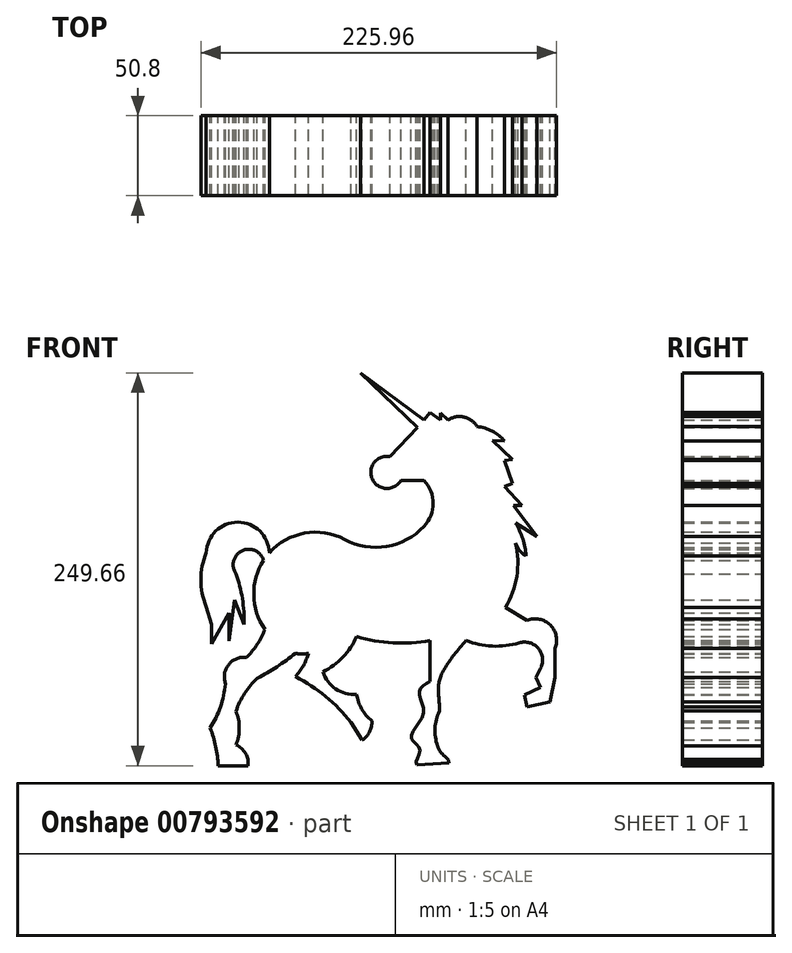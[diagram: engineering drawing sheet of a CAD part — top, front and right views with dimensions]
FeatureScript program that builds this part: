
annotation { "Feature Type Name" : "Feature", "Feature Type Description" : "" }
export const myFeature = defineFeature(function(context is Context, id is Id, definition is map)
    precondition{}
    {
        {
            var Q0;
            Q0=qCreatedBy(makeId("Front.planeOp"),FACE);
            var sketch = newSketch(context, id + "F0", { "sketchPlane" : qUnion([Q0])});
            skLineSegment(sketch, "E0", {"start": v(117.02, 256.9) * mm, "end": v(157.35, 226.79) * mm});
            skLineSegment(sketch, "E1", {"start": v(117.02, 256.9) * mm, "end": v(153.27, 222.2) * mm});
            skLineSegment(sketch, "E2", {"start": v(153.27, 222.2) * mm, "end": v(135.55, 203.69) * mm});
            skArc(sketch, "E3", {"start": v(135.55, 203.69) * mm, "mid": v(124.47, 189.38) * mm, "end": v(142.55, 188.5) * mm});
            skLineSegment(sketch, "E4", {"start": v(142.55, 188.5) * mm, "end": v(157.35, 188.5) * mm});
            skArc(sketch, "E5", {"start": v(157.35, 159.4) * mm, "mid": v(163.1, 173.94) * mm, "end": v(157.35, 188.5) * mm});
            skArc(sketch, "E6", {"start": v(106.85, 151.02) * mm, "mid": v(59.08, 142.48) * mm, "end": v(56.24, 94.04) * mm});
            skArc(sketch, "E7", {"start": v(106.85, 151.02) * mm, "mid": v(133.52, 146.63) * mm, "end": v(157.35, 159.4) * mm});
            skArc(sketch, "E8", {"start": v(208.92, 107.83) * mm, "mid": v(216.22, 127.6) * mm, "end": v(215.55, 148.67) * mm});
            skArc(sketch, "E9", {"start": v(183.9, 86.9) * mm, "mid": v(200.68, 83.25) * mm, "end": v(217.72, 85.39) * mm});
            skArc(sketch, "E10", {"start": v(231.43, 69.23) * mm, "mid": v(229.88, 81.8) * mm, "end": v(217.72, 85.39) * mm});
            skArc(sketch, "E11", {"start": v(240.57, 81.8) * mm, "mid": v(237.5, 96.6) * mm, "end": v(222.7, 99.66) * mm});
            skLineSegment(sketch, "E12", {"start": v(240.57, 81.8) * mm, "end": v(240.57, 63.41) * mm});
            skLineSegment(sketch, "E13", {"start": v(208.92, 107.83) * mm, "end": v(222.7, 99.66) * mm});
            skLineSegment(sketch, "E14", {"start": v(231.43, 69.23) * mm, "end": v(228.56, 63.41) * mm});
            skLineSegment(sketch, "E15", {"start": v(228.56, 63.41) * mm, "end": v(231.43, 57) * mm});
            skLineSegment(sketch, "E16", {"start": v(231.43, 57) * mm, "end": v(221.07, 52.36) * mm});
            skLineSegment(sketch, "E17", {"start": v(221.07, 52.36) * mm, "end": v(222.7, 44.75) * mm});
            skLineSegment(sketch, "E18", {"start": v(222.7, 44.75) * mm, "end": v(237.34, 47.87) * mm});
            skLineSegment(sketch, "E19", {"start": v(237.34, 47.87) * mm, "end": v(240.57, 63.41) * mm});
            skArc(sketch, "E20", {"start": v(59.08, 142.48) * mm, "mid": v(39.04, 161.99) * mm, "end": v(19, 142.48) * mm});
            skPoint(sketch, "E20.endSnap0", {"position": v(59.08, 142.48) * mm});
            skArc(sketch, "E21", {"start": v(55.46, 137.72) * mm, "mid": v(41.7, 143.82) * mm, "end": v(37.88, 129.27) * mm});
            skArc(sketch, "E22", {"start": v(19, 142.48) * mm, "mid": v(15.58, 125.41) * mm, "end": v(19, 108.34) * mm});
            skArc(sketch, "E23", {"start": v(44.52, 76.17) * mm, "mid": v(33.18, 71.46) * mm, "end": v(31.25, 59.33) * mm});
            skArc(sketch, "E24", {"start": v(114.47, 89.45) * mm, "mid": v(137.67, 85.34) * mm, "end": v(161.2, 86.84) * mm});
            skArc(sketch, "E25", {"start": v(93.02, 66.98) * mm, "mid": v(105.8, 76.26) * mm, "end": v(114.47, 89.45) * mm});
            skArc(sketch, "E26", {"start": v(93.02, 66.98) * mm, "mid": v(101.25, 56.1) * mm, "end": v(114.47, 52.69) * mm});
            skArc(sketch, "E27", {"start": v(114.47, 52.69) * mm, "mid": v(117.73, 43.35) * mm, "end": v(124.17, 35.84) * mm});
            skArc(sketch, "E28", {"start": v(118.04, 23.59) * mm, "mid": v(122.8, 28.87) * mm, "end": v(124.17, 35.84) * mm});
            skArc(sketch, "E29", {"start": v(167.05, 61.35) * mm, "mid": v(177.73, 72.64) * mm, "end": v(183.9, 86.9) * mm});
            skArc(sketch, "E30", {"start": v(167.05, 41.98) * mm, "mid": v(169.24, 51.67) * mm, "end": v(167.05, 61.35) * mm});
            skArc(sketch, "E31", {"start": v(167.05, 41.98) * mm, "mid": v(164.24, 29.59) * mm, "end": v(167.05, 17.2) * mm});
            skArc(sketch, "E32", {"start": v(173.17, 9.02) * mm, "mid": v(171.2, 13.93) * mm, "end": v(167.05, 17.2) * mm});
            skLineSegment(sketch, "E33", {"start": v(152.75, 7.8) * mm, "end": v(173.17, 9.02) * mm});
            skLineSegment(sketch, "E34", {"start": v(161.2, 86.84) * mm, "end": v(161.2, 60.95) * mm});
            skFitSpline(sketch, "E35", {"points": [v(161.2, 60.95) * mm, v(154.29, 54.22) * mm, v(156.84, 40.44) * mm, v(149.18, 25.12) * mm, v(154.8, 17.46) * mm, v(152.75, 7.8) * mm, v(173.17, 9.02) * mm, v(167.05, 17.2) * mm, v(167.05, 41.98) * mm, v(167.05, 61.35) * mm, v(183.9, 86.9) * mm], "startDerivative": vector(-126.82, -72.82) * mm, "endDerivative": vector(160.9, 190.3) * mm});
            skArc(sketch, "E36", {"start": v(44.52, 76.17) * mm, "mid": v(51.4, 84.44) * mm, "end": v(56.24, 94.04) * mm});
            skArc(sketch, "E37", {"start": v(21.55, 31.25) * mm, "mid": v(28.01, 44.73) * mm, "end": v(31.25, 59.33) * mm});
            skArc(sketch, "E38", {"start": v(26.65, 7.25) * mm, "mid": v(25.03, 19.45) * mm, "end": v(21.55, 31.25) * mm});
            skLineSegment(sketch, "E39", {"start": v(26.65, 7.25) * mm, "end": v(45.54, 7.25) * mm});
            skArc(sketch, "E40", {"start": v(51.4, 62.9) * mm, "mid": v(63.94, 70.18) * mm, "end": v(75.66, 78.73) * mm});
            skPoint(sketch, "E40.startSnap0", {"position": v(51.4, 84.44) * mm});
            skArc(sketch, "E41", {"start": v(75.66, 78.73) * mm, "mid": v(79.75, 78.22) * mm, "end": v(83.83, 78.73) * mm});
            skArc(sketch, "E42", {"start": v(75.66, 63.92) * mm, "mid": v(80.62, 70.84) * mm, "end": v(83.83, 78.73) * mm});
            skArc(sketch, "E43", {"start": v(110.9, 34.82) * mm, "mid": v(94.88, 51.31) * mm, "end": v(75.66, 63.92) * mm});
            skLineSegment(sketch, "E44", {"start": v(110.9, 34.82) * mm, "end": v(118.04, 23.59) * mm});
            skArc(sketch, "E45", {"start": v(51.4, 62.9) * mm, "mid": v(43.37, 53.26) * mm, "end": v(37.88, 41.97) * mm});
            skArc(sketch, "E46", {"start": v(37.88, 20.52) * mm, "mid": v(39.97, 31.25) * mm, "end": v(37.88, 41.97) * mm});
            skArc(sketch, "E47", {"start": v(45.54, 7.25) * mm, "mid": v(43.99, 15.2) * mm, "end": v(37.88, 20.52) * mm});
            skArc(sketch, "E48", {"start": v(215.55, 148.67) * mm, "mid": v(218.09, 143.95) * mm, "end": v(222.2, 140.5) * mm});
            skArc(sketch, "E49", {"start": v(222.2, 140.5) * mm, "mid": v(220.05, 151.34) * mm, "end": v(215.55, 161.44) * mm});
            skLineSegment(sketch, "E50", {"start": v(157.35, 226.79) * mm, "end": v(161.08, 231.77) * mm});
            skLineSegment(sketch, "E51", {"start": v(161.08, 231.77) * mm, "end": v(167.75, 226.79) * mm});
            skLineSegment(sketch, "E52", {"start": v(167.75, 226.79) * mm, "end": v(167.75, 231.38) * mm});
            skLineSegment(sketch, "E53", {"start": v(167.75, 231.38) * mm, "end": v(172.55, 226.79) * mm});
            skArc(sketch, "E54", {"start": v(191.05, 222.7) * mm, "mid": v(182.7, 228.81) * mm, "end": v(172.55, 226.79) * mm});
            skArc(sketch, "E55", {"start": v(208.4, 213.51) * mm, "mid": v(200.64, 219.82) * mm, "end": v(191.05, 222.7) * mm});
            skLineSegment(sketch, "E56", {"start": v(200.64, 214.02) * mm, "end": v(208.4, 213.51) * mm});
            skPoint(sketch, "E56.startSnap0", {"position": v(200.64, 219.82) * mm});
            skLineSegment(sketch, "E57", {"start": v(200.64, 214.02) * mm, "end": v(213.51, 201.77) * mm});
            skLineSegment(sketch, "E58", {"start": v(213.51, 201.77) * mm, "end": v(208.4, 201.31) * mm});
            skLineSegment(sketch, "E59", {"start": v(208.4, 201.31) * mm, "end": v(213.51, 186.45) * mm});
            skLineSegment(sketch, "E60", {"start": v(213.51, 186.45) * mm, "end": v(208.4, 184.7) * mm});
            skLineSegment(sketch, "E61", {"start": v(208.4, 184.7) * mm, "end": v(219.64, 172.67) * mm});
            skLineSegment(sketch, "E62", {"start": v(219.64, 172.67) * mm, "end": v(214.02, 172.67) * mm});
            skPoint(sketch, "E62.endSnap0", {"position": v(214.02, 178.68) * mm});
            skLineSegment(sketch, "E63", {"start": v(214.02, 172.67) * mm, "end": v(229.08, 152.88) * mm});
            skLineSegment(sketch, "E64", {"start": v(229.08, 152.88) * mm, "end": v(215.55, 161.44) * mm});
            skArc(sketch, "E65", {"start": v(43.12, 97.11) * mm, "mid": v(41.95, 113.43) * mm, "end": v(37.88, 129.27) * mm});
            skLineSegment(sketch, "E66", {"start": v(43.12, 97.11) * mm, "end": v(36.91, 112.47) * mm});
            skLineSegment(sketch, "E67", {"start": v(36.91, 112.47) * mm, "end": v(33.45, 86.7) * mm});
            skLineSegment(sketch, "E68", {"start": v(33.45, 86.7) * mm, "end": v(33.45, 104.26) * mm});
            skLineSegment(sketch, "E69", {"start": v(33.45, 104.26) * mm, "end": v(22.3, 84.75) * mm});
            skLineSegment(sketch, "E70", {"start": v(22.3, 84.75) * mm, "end": v(22.3, 97.11) * mm});
            skLineSegment(sketch, "E71", {"start": v(22.3, 97.11) * mm, "end": v(19, 108.34) * mm});
            skSolve(sketch);
        }
        {
            var Q0;
            Q0=makeQuery(id+"F0.imprint","IMPRINT",FACE,{"disambiguationData":[TD([[makeQuery(id+"F0.imprint","IMPRINT",EDGE,{"derivedFrom":sQuery(id+"F0.wireOp",EDGE,"E0")}),-1.0]])]});
            var Q1;
            {var subQ0=sQuery(id+"F0.wireOp",EDGE,"E20");Q1=makeQuery(id+"F0.imprint","IMPRINT",FACE,{"disambiguationData":[TD([[makeQuery(id+"F0.imprint","IMPRINT",EDGE,{"derivedFrom":subQ0}),1.0]])]});}
            extrude(context, id + "F1", {"entities" : qUnion([Q0, Q1]), "depth" : 50.8 * mm, "offsetDistance" : 25.4 * mm});
        }
    });
